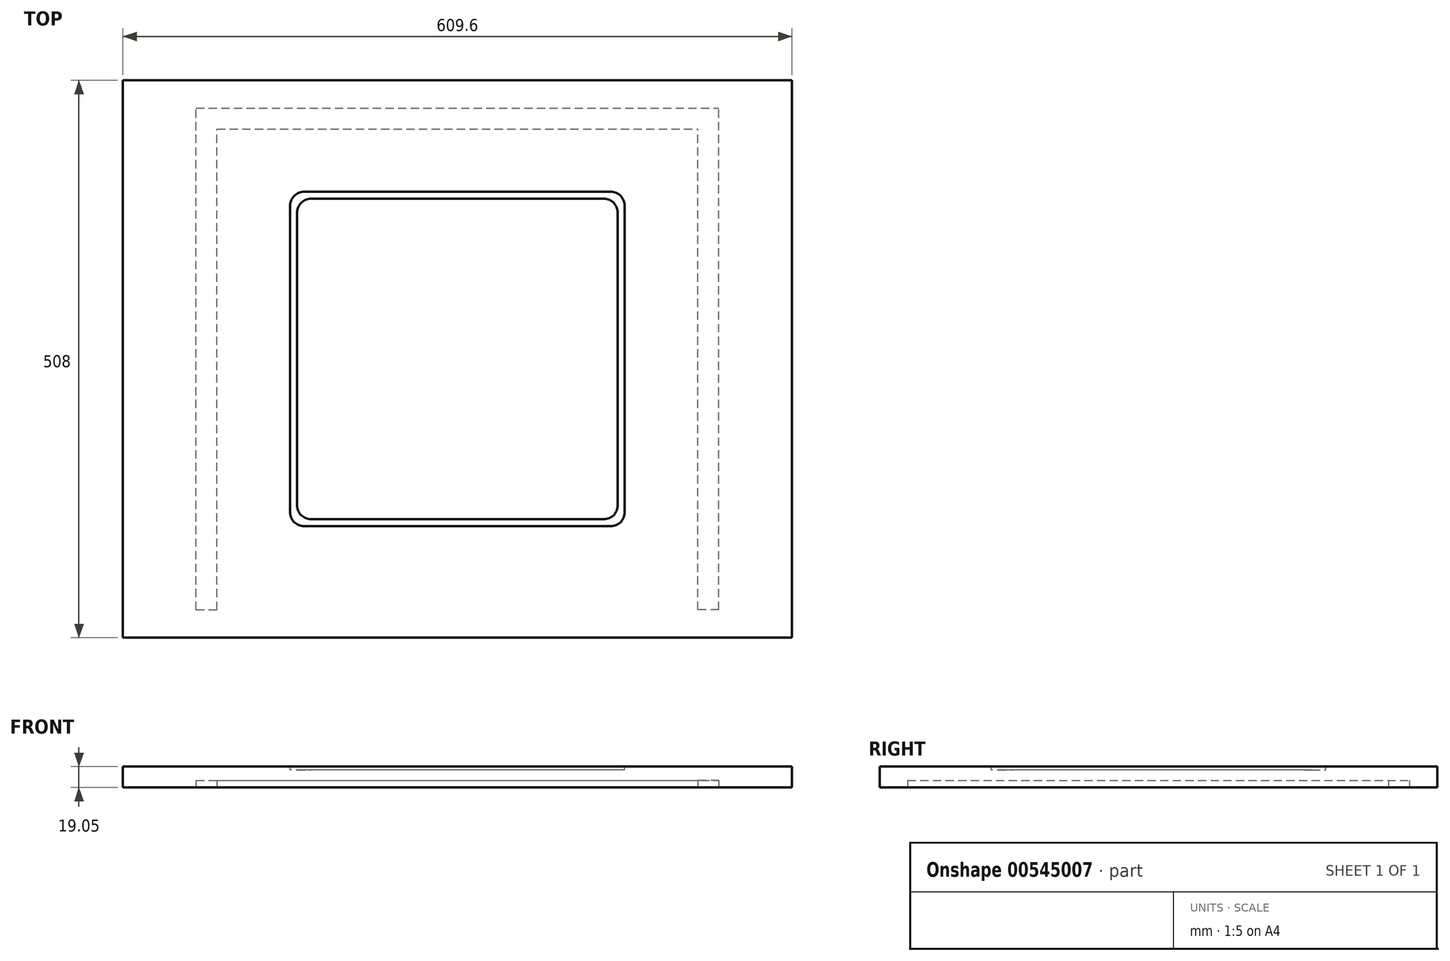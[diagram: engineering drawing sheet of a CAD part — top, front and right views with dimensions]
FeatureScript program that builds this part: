
annotation { "Feature Type Name" : "Feature", "Feature Type Description" : "" }
export const myFeature = defineFeature(function(context is Context, id is Id, definition is map)
    precondition{}
    {
        {
            var Q0;
            Q0=qCreatedBy(makeId("Top.planeOp"),FACE);
            var sketch = newSketch(context, id + "F0", { "sketchPlane" : qUnion([Q0])});
            skLineSegment(sketch, "E0.bottom", {"start": v(304.8, 254) * mm, "end": v(-304.8, 254) * mm});
            skLineSegment(sketch, "E0.top", {"start": v(304.8, -254) * mm, "end": v(-304.8, -254) * mm});
            skLineSegment(sketch, "E0.left", {"start": v(304.8, 254) * mm, "end": v(304.8, -254) * mm});
            skLineSegment(sketch, "E0.right", {"start": v(-304.8, 254) * mm, "end": v(-304.8, -254) * mm});
            skPoint(sketch, "E0.middle", {"position": v(0, 0) * mm});
            skSolve(sketch);
        }
        {
            var Q0;
            Q0 = qSketchRegion(id + "F0", true);
            extrude(context, id + "F1", {"entities" : qUnion([Q0]), "depth" : 19.05 * mm, "offsetDistance" : 25.4 * mm});
        }
        {
            var Q0;
            Q0=makeQuery(id+"F1.opExtrude","CAP_FACE",FACE,{"disambiguationData":[OSD([sQuery(id+"F0.wireOp",EDGE,"E0.bottom"),sQuery(id+"F0.wireOp",EDGE,"E0.top"),sQuery(id+"F0.wireOp",EDGE,"E0.left"),sQuery(id+"F0.wireOp",EDGE,"E0.right")])],"isStart":false});
            var sketch = newSketch(context, id + "F2", { "sketchPlane" : qUnion([Q0])});
            skLineSegment(sketch, "E1.bottom", {"start": v(139.7, 152.4) * mm, "end": v(-139.7, 152.4) * mm});
            skLineSegment(sketch, "E1.top", {"start": v(139.7, -152.4) * mm, "end": v(-139.7, -152.4) * mm});
            skLineSegment(sketch, "E1.left", {"start": v(152.4, 139.7) * mm, "end": v(152.4, -139.7) * mm});
            skLineSegment(sketch, "E1.right", {"start": v(-152.4, 139.7) * mm, "end": v(-152.4, -139.7) * mm});
            skPoint(sketch, "E1.middle", {"position": v(0, 0) * mm});
            skPoint(sketch, "E2.visualSharp", {"position": v(-152.4, 152.4) * mm});
            skArc(sketch, "E2.filletArc", {"start": v(-139.7, 152.4) * mm, "mid": v(-148.68, 148.68) * mm, "end": v(-152.4, 139.7) * mm});
            skPoint(sketch, "E3.visualSharp", {"position": v(152.4, 152.4) * mm});
            skArc(sketch, "E3.filletArc", {"start": v(152.4, 139.7) * mm, "mid": v(148.68, 148.68) * mm, "end": v(139.7, 152.4) * mm});
            skPoint(sketch, "E4.visualSharp", {"position": v(152.4, -152.4) * mm});
            skArc(sketch, "E4.filletArc", {"start": v(139.7, -152.4) * mm, "mid": v(148.68, -148.68) * mm, "end": v(152.4, -139.7) * mm});
            skPoint(sketch, "E5.visualSharp", {"position": v(-152.4, -152.4) * mm});
            skArc(sketch, "E5.filletArc", {"start": v(-152.4, -139.7) * mm, "mid": v(-148.68, -148.68) * mm, "end": v(-139.7, -152.4) * mm});
            skSolve(sketch);
        }
        {
            var Q0;
            Q0 = qSketchRegion(id + "F2", true);
            extrude(context, id + "F3", {"entities" : qUnion([Q0]), "operationType" : NewBodyOperationType.REMOVE, "oppositeDirection" : true, "depth" : 3.17 * mm, "offsetDistance" : 25.4 * mm});
        }
        {
            var Q0;
            Q0=makeQuery(id+"F3.boolean.opBoolean","COPY",FACE,{"derivedFrom":makeQuery(id+"F3.opExtrude","CAP_FACE",FACE,{"disambiguationData":[OSD([sQuery(id+"F2.wireOp",EDGE,"E1.bottom"),sQuery(id+"F2.wireOp",EDGE,"E1.top"),sQuery(id+"F2.wireOp",EDGE,"E1.left"),sQuery(id+"F2.wireOp",EDGE,"E1.right")])],"isStart":false})});
            var sketch = newSketch(context, id + "F4", { "sketchPlane" : qUnion([Q0])});
            skLineSegment(sketch, "E6.bottom", {"start": v(133.35, 146.05) * mm, "end": v(-133.35, 146.05) * mm});
            skLineSegment(sketch, "E6.top", {"start": v(133.35, -146.05) * mm, "end": v(-133.35, -146.05) * mm});
            skLineSegment(sketch, "E6.left", {"start": v(146.05, 133.35) * mm, "end": v(146.05, -133.35) * mm});
            skLineSegment(sketch, "E6.right", {"start": v(-146.05, 133.35) * mm, "end": v(-146.05, -133.35) * mm});
            skPoint(sketch, "E6.middle", {"position": v(0, 0) * mm});
            skPoint(sketch, "E7.visualSharp", {"position": v(-146.05, 146.05) * mm});
            skArc(sketch, "E7.filletArc", {"start": v(-133.35, 146.05) * mm, "mid": v(-142.33, 142.33) * mm, "end": v(-146.05, 133.35) * mm});
            skPoint(sketch, "E8.visualSharp", {"position": v(146.05, 146.05) * mm});
            skArc(sketch, "E8.filletArc", {"start": v(146.05, 133.35) * mm, "mid": v(142.33, 142.33) * mm, "end": v(133.35, 146.05) * mm});
            skPoint(sketch, "E9.visualSharp", {"position": v(146.05, -146.05) * mm});
            skArc(sketch, "E9.filletArc", {"start": v(133.35, -146.05) * mm, "mid": v(142.33, -142.33) * mm, "end": v(146.05, -133.35) * mm});
            skPoint(sketch, "E10.visualSharp", {"position": v(-146.05, -146.05) * mm});
            skArc(sketch, "E10.filletArc", {"start": v(-146.05, -133.35) * mm, "mid": v(-142.33, -142.33) * mm, "end": v(-133.35, -146.05) * mm});
            skSolve(sketch);
        }
        {
            var Q0;
            Q0 = qSketchRegion(id + "F4", true);
            extrude(context, id + "F5", {"entities" : qUnion([Q0]), "operationType" : NewBodyOperationType.REMOVE, "oppositeDirection" : true, "depth" : 3 / 101.6 * mm, "offsetDistance" : 25.4 * mm});
        }
        {
            var Q0;
            Q0=makeQuery(id+"F1.opExtrude","CAP_FACE",FACE,{"disambiguationData":[OSD([sQuery(id+"F0.wireOp",EDGE,"E0.bottom"),sQuery(id+"F0.wireOp",EDGE,"E0.top"),sQuery(id+"F0.wireOp",EDGE,"E0.left"),sQuery(id+"F0.wireOp",EDGE,"E0.right")])],"isStart":true});
            var sketch = newSketch(context, id + "F6", { "sketchPlane" : qUnion([Q0])});
            skLineSegment(sketch, "E11.bottom", {"start": v(228.6, 228.6) * mm, "end": v(-228.6, 228.6) * mm, "construction": true});
            skLineSegment(sketch, "E11.top", {"start": v(228.6, -228.6) * mm, "end": v(-228.6, -228.6) * mm, "construction": true});
            skLineSegment(sketch, "E11.left", {"start": v(228.6, 228.6) * mm, "end": v(228.6, -228.6) * mm, "construction": true});
            skLineSegment(sketch, "E11.right", {"start": v(-228.6, 228.6) * mm, "end": v(-228.6, -228.6) * mm, "construction": true});
            skPoint(sketch, "E11.middle", {"position": v(0, 0) * mm});
            skLineSegment(sketch, "E12.bottom", {"start": v(-238.13, 228.6) * mm, "end": v(-219.08, 228.6) * mm});
            skLineSegment(sketch, "E12.top", {"start": v(-238.12, -228.6) * mm, "end": v(-219.07, -228.6) * mm});
            skLineSegment(sketch, "E12.left", {"start": v(-238.12, 228.6) * mm, "end": v(-238.12, -228.6) * mm});
            skLineSegment(sketch, "E12.right", {"start": v(-219.07, 228.6) * mm, "end": v(-219.07, -228.6) * mm});
            skLineSegment(sketch, "E13.MirrorCS", {"start": v(219.07, 228.6) * mm, "end": v(219.07, -228.6) * mm});
            skLineSegment(sketch, "E14.MirrorCS", {"start": v(238.12, 228.6) * mm, "end": v(238.12, -228.6) * mm});
            skLineSegment(sketch, "E15.MirrorCS", {"start": v(238.13, 228.6) * mm, "end": v(219.08, 228.6) * mm});
            skLineSegment(sketch, "E16.MirrorCS", {"start": v(238.12, -228.6) * mm, "end": v(219.07, -228.6) * mm});
            skLineSegment(sketch, "E17.bottom", {"start": v(-219.07, -228.6) * mm, "end": v(219.07, -228.6) * mm});
            skLineSegment(sketch, "E17.top", {"start": v(-219.07, -209.55) * mm, "end": v(219.07, -209.55) * mm});
            skLineSegment(sketch, "E17.left", {"start": v(-219.07, -228.6) * mm, "end": v(-219.07, -209.55) * mm});
            skLineSegment(sketch, "E17.right", {"start": v(219.07, -228.6) * mm, "end": v(219.07, -209.55) * mm});
            skSolve(sketch);
        }
        {
            var Q0;
            Q0 = qSketchRegion(id + "F6", true);
            extrude(context, id + "F7", {"entities" : qUnion([Q0]), "operationType" : NewBodyOperationType.REMOVE, "oppositeDirection" : true, "depth" : 6.35 * mm, "offsetDistance" : 25.4 * mm});
        }
    });
